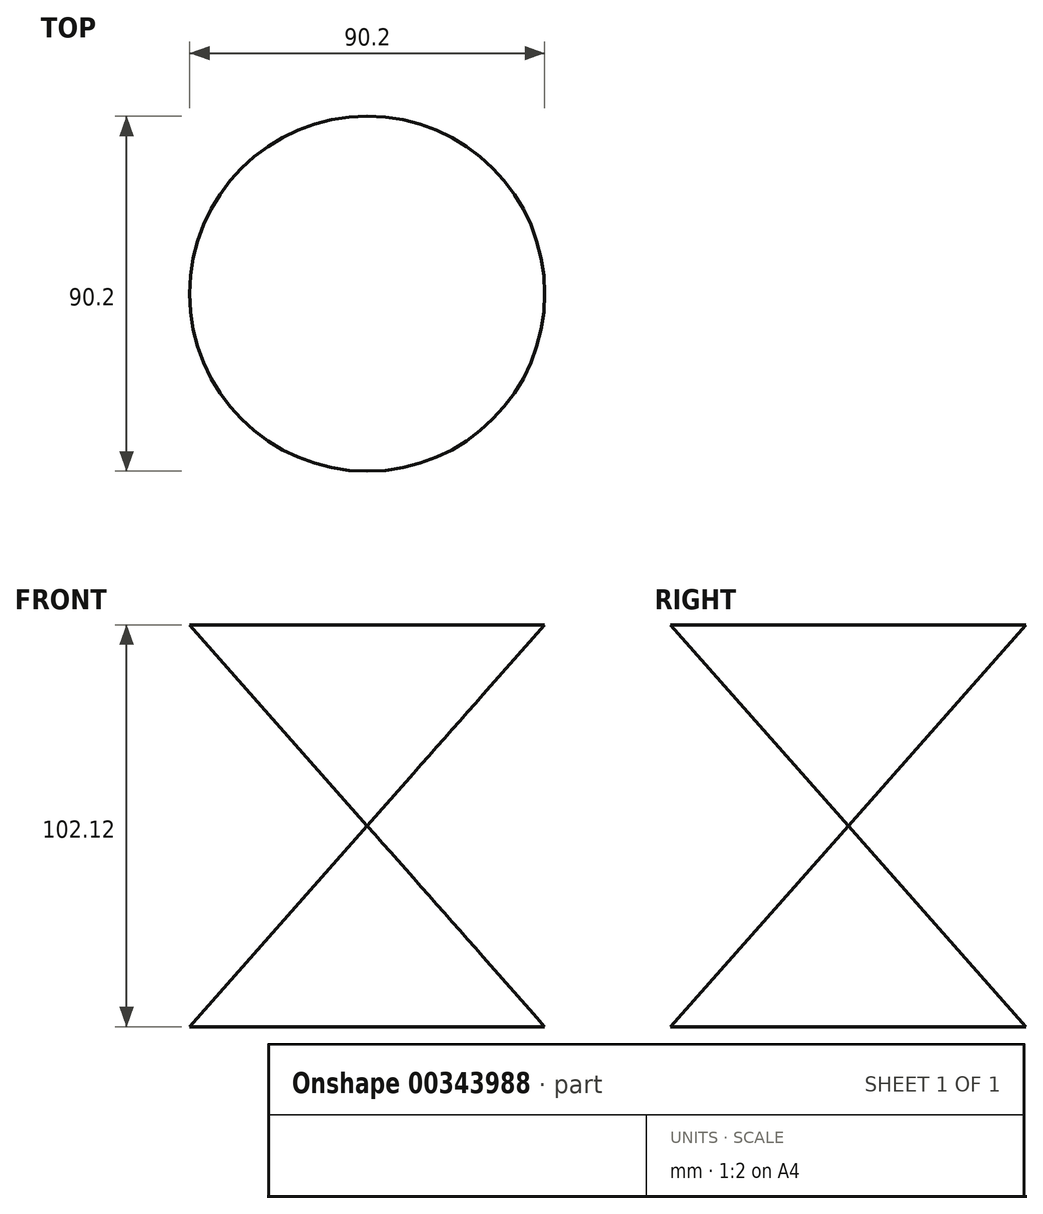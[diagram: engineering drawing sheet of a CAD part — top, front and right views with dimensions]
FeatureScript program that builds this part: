
annotation { "Feature Type Name" : "Feature", "Feature Type Description" : "" }
export const myFeature = defineFeature(function(context is Context, id is Id, definition is map)
    precondition{}
    {
        {
            var Q0;
            Q0=qCreatedBy(makeId("Front.planeOp"),FACE);
            var sketch = newSketch(context, id + "F0", { "sketchPlane" : qUnion([Q0])});
            skLineSegment(sketch, "E0", {"start": v(0, 0) * mm, "end": v(-45.1, 51.06) * mm});
            skLineSegment(sketch, "E1", {"start": v(0, 0) * mm, "end": v(0, 52.54) * mm});
            skSolve(sketch);
        }
        {
            var Q0;
            Q0=sQuery(id+"F0.wireOp",EDGE,"E0");
            var Q1;
            Q1=sQuery(id+"F0.wireOp",EDGE,"E1");
            revolve(context, id + "F1", {"bodyType" : ToolBodyType.SURFACE, "surfaceEntities" : qUnion([Q0]), "axis" : qUnion([Q1]), "revolveType" : RevolveType.FULL});
        }
        {
            var Q0;
            Q0=makeQuery(id+"F1.opRevolve","SWEPT_BODY",BODY,{"disambiguationData":[OSD([sQuery(id+"F0.wireOp",EDGE,"E0")])]});
            var Q1;
            Q1=qCreatedBy(makeId("Top.planeOp"),FACE);
            mirror(context, id + "F2", {"entities" : qUnion([Q0]), "mirrorPlane" : qUnion([Q1])});
        }
    });
